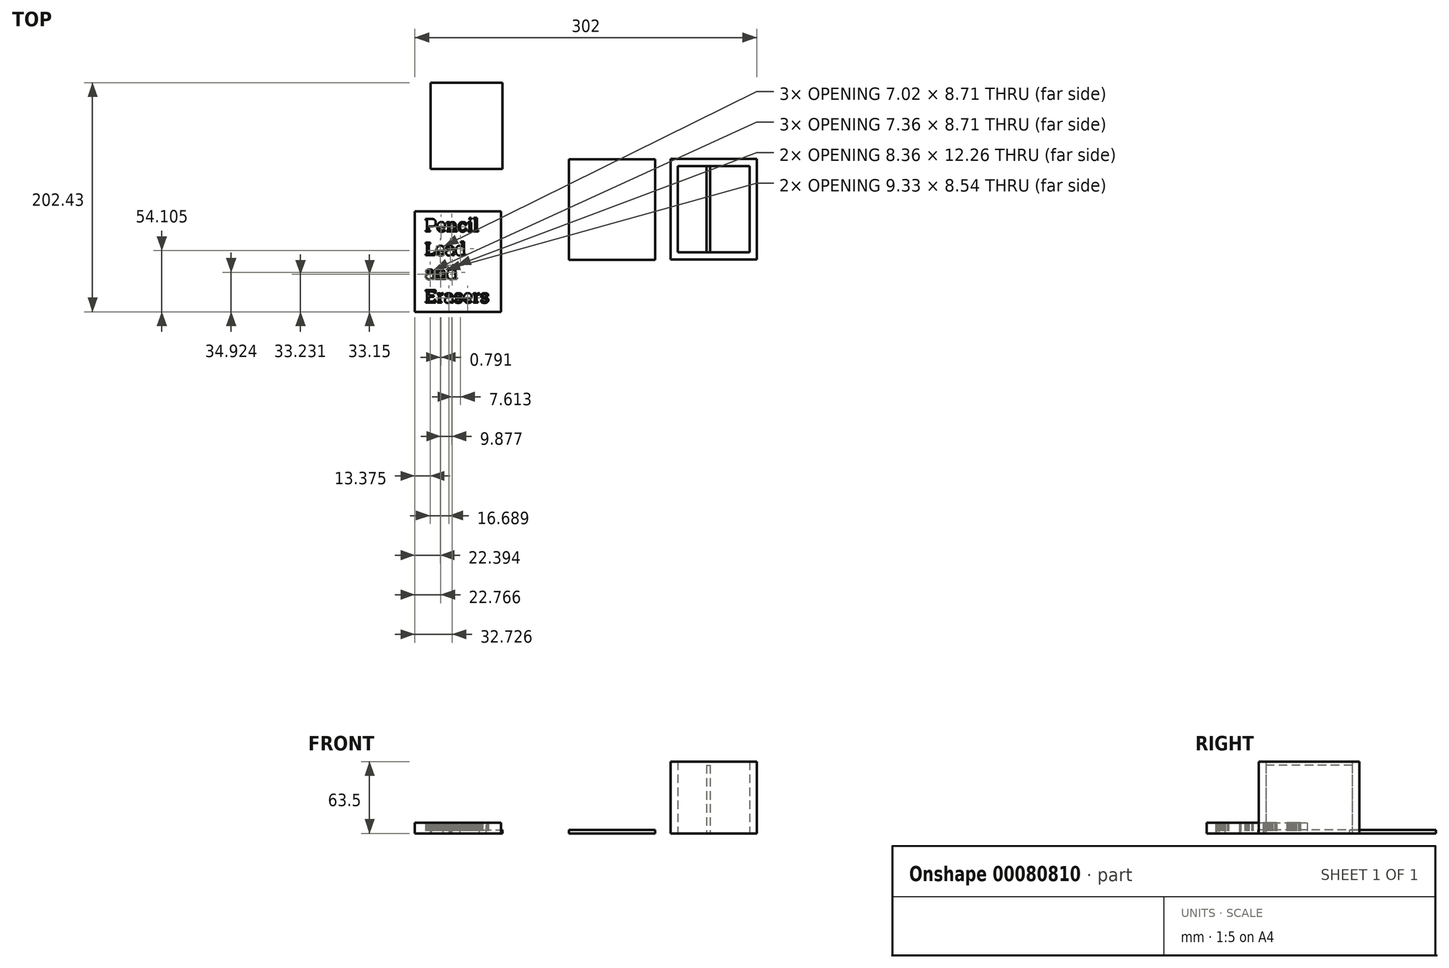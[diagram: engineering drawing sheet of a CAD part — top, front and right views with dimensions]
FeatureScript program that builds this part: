
annotation { "Feature Type Name" : "Feature", "Feature Type Description" : "" }
export const myFeature = defineFeature(function(context is Context, id is Id, definition is map)
    precondition{}
    {
        {
            var Q0;
            Q0=qCreatedBy(makeId("Top.planeOp"),FACE);
            var sketch = newSketch(context, id + "F0", { "sketchPlane" : qUnion([Q0])});
            skLineSegment(sketch, "E0.bottom", {"start": v(-60.14, 45.79) * mm, "end": v(16.06, 45.79) * mm});
            skLineSegment(sketch, "E0.top", {"start": v(-60.14, -43.11) * mm, "end": v(16.06, -43.11) * mm});
            skLineSegment(sketch, "E0.left", {"start": v(-60.14, 45.79) * mm, "end": v(-60.14, -43.11) * mm});
            skLineSegment(sketch, "E0.right", {"start": v(16.06, 45.79) * mm, "end": v(16.06, -43.11) * mm});
            skLineSegment(sketch, "E1.bottom", {"start": v(29.74, 46.15) * mm, "end": v(105.94, 46.15) * mm});
            skLineSegment(sketch, "E1.top", {"start": v(29.74, -42.75) * mm, "end": v(105.94, -42.75) * mm});
            skLineSegment(sketch, "E1.left", {"start": v(29.74, 46.15) * mm, "end": v(29.74, -42.75) * mm});
            skLineSegment(sketch, "E1.right", {"start": v(105.94, 46.15) * mm, "end": v(105.94, -42.75) * mm});
            skLineSegment(sketch, "E2.bottom", {"start": v(36.09, 39.8) * mm, "end": v(61.49, 39.8) * mm});
            skLineSegment(sketch, "E2.top", {"start": v(36.09, -36.4) * mm, "end": v(61.49, -36.4) * mm});
            skLineSegment(sketch, "E2.left", {"start": v(36.09, 39.8) * mm, "end": v(36.09, -36.4) * mm});
            skLineSegment(sketch, "E2.right", {"start": v(61.49, 39.8) * mm, "end": v(61.49, -36.4) * mm});
            skLineSegment(sketch, "E3.bottom", {"start": v(-196.06, -88.9) * mm, "end": v(-119.86, -88.9) * mm});
            skLineSegment(sketch, "E3.top", {"start": v(-196.06, 0) * mm, "end": v(-119.86, 0) * mm});
            skLineSegment(sketch, "E3.left", {"start": v(-196.06, -88.9) * mm, "end": v(-196.06, 0) * mm});
            skLineSegment(sketch, "E3.right", {"start": v(-119.86, -88.9) * mm, "end": v(-119.86, 0) * mm});
            skLineSegment(sketch, "E4.bottom", {"start": v(-182.16, 37.33) * mm, "end": v(-118.66, 37.33) * mm});
            skLineSegment(sketch, "E4.top", {"start": v(-182.16, 113.53) * mm, "end": v(-118.66, 113.53) * mm});
            skLineSegment(sketch, "E4.left", {"start": v(-182.16, 37.33) * mm, "end": v(-182.16, 113.53) * mm});
            skLineSegment(sketch, "E4.right", {"start": v(-118.66, 37.33) * mm, "end": v(-118.66, 113.53) * mm});
            skLineSegment(sketch, "E5.bottom", {"start": v(64.66, 39.8) * mm, "end": v(99.59, 39.8) * mm});
            skLineSegment(sketch, "E5.top", {"start": v(64.66, -36.4) * mm, "end": v(99.59, -36.4) * mm});
            skLineSegment(sketch, "E5.left", {"start": v(64.66, 39.8) * mm, "end": v(64.66, -36.4) * mm});
            skLineSegment(sketch, "E5.right", {"start": v(99.59, 39.8) * mm, "end": v(99.59, -36.4) * mm});
            skLineSegment(sketch, "E6", {"start": v(61.49, 39.8) * mm, "end": v(64.66, 39.8) * mm});
            skLineSegment(sketch, "E7", {"start": v(61.49, -36.4) * mm, "end": v(64.66, -36.4) * mm});
            skText(sketch, "E8", { "text": "Pencil\nLead\nand\nErasers", "fontName": "RobotoSlab-Regular.ttf"});
            const initialGuessF0  = {"E8": [-0.18717, -0.01803, 1, 0, 0.01143]};
            skSetInitialGuess(sketch, initialGuessF0);
            skSolve(sketch);
        }
        {
            var Q0;
            Q0=makeQuery(id+"F0.imprint","IMPRINT",FACE,{"disambiguationData":[TD([[makeQuery(id+"F0.imprint","IMPRINT",EDGE,{"derivedFrom":sQuery(id+"F0.wireOp",EDGE,"E3.bottom")}),1.0]])]});
            extrude(context, id + "F1", {"entities" : qUnion([Q0]), "depth" : 9.52 * mm});
        }
        {
            var Q0;
            Q0=makeQuery(id+"F0.imprint","IMPRINT",FACE,{"disambiguationData":[TD([[makeQuery(id+"F0.imprint","IMPRINT",EDGE,{"derivedFrom":sQuery(id+"F0.wireOp",EDGE,"E4.bottom")}),1.0]])]});
            var Q1;
            Q1=makeQuery(id+"F0.imprint","IMPRINT",FACE,{"disambiguationData":[TD([[makeQuery(id+"F0.imprint","IMPRINT",EDGE,{"derivedFrom":sQuery(id+"F0.wireOp",EDGE,"E0.bottom")}),-1.0]])]});
            extrude(context, id + "F2", {"entities" : qUnion([Q0, Q1]), "depth" : 3.17 * mm});
        }
        {
            var Q0;
            Q0=makeQuery(id+"F0.imprint","IMPRINT",FACE,{"disambiguationData":[TD([[makeQuery(id+"F0.imprint","IMPRINT",EDGE,{"derivedFrom":sQuery(id+"F0.wireOp",EDGE,"E1.bottom")}),-1.0]])]});
            extrude(context, id + "F3", {"entities" : qUnion([Q0]), "depth" : 63.5 * mm});
        }
        {
            var Q0;
            Q0=makeQuery(id+"F0.imprint","IMPRINT",FACE,{"disambiguationData":[TD([[makeQuery(id+"F0.imprint","IMPRINT",EDGE,{"derivedFrom":sQuery(id+"F0.wireOp",EDGE,"E2.right")}),1.0]])]});
            extrude(context, id + "F4", {"entities" : qUnion([Q0]), "operationType" : NewBodyOperationType.ADD, "depth" : 60.32 * mm});
        }
    });
